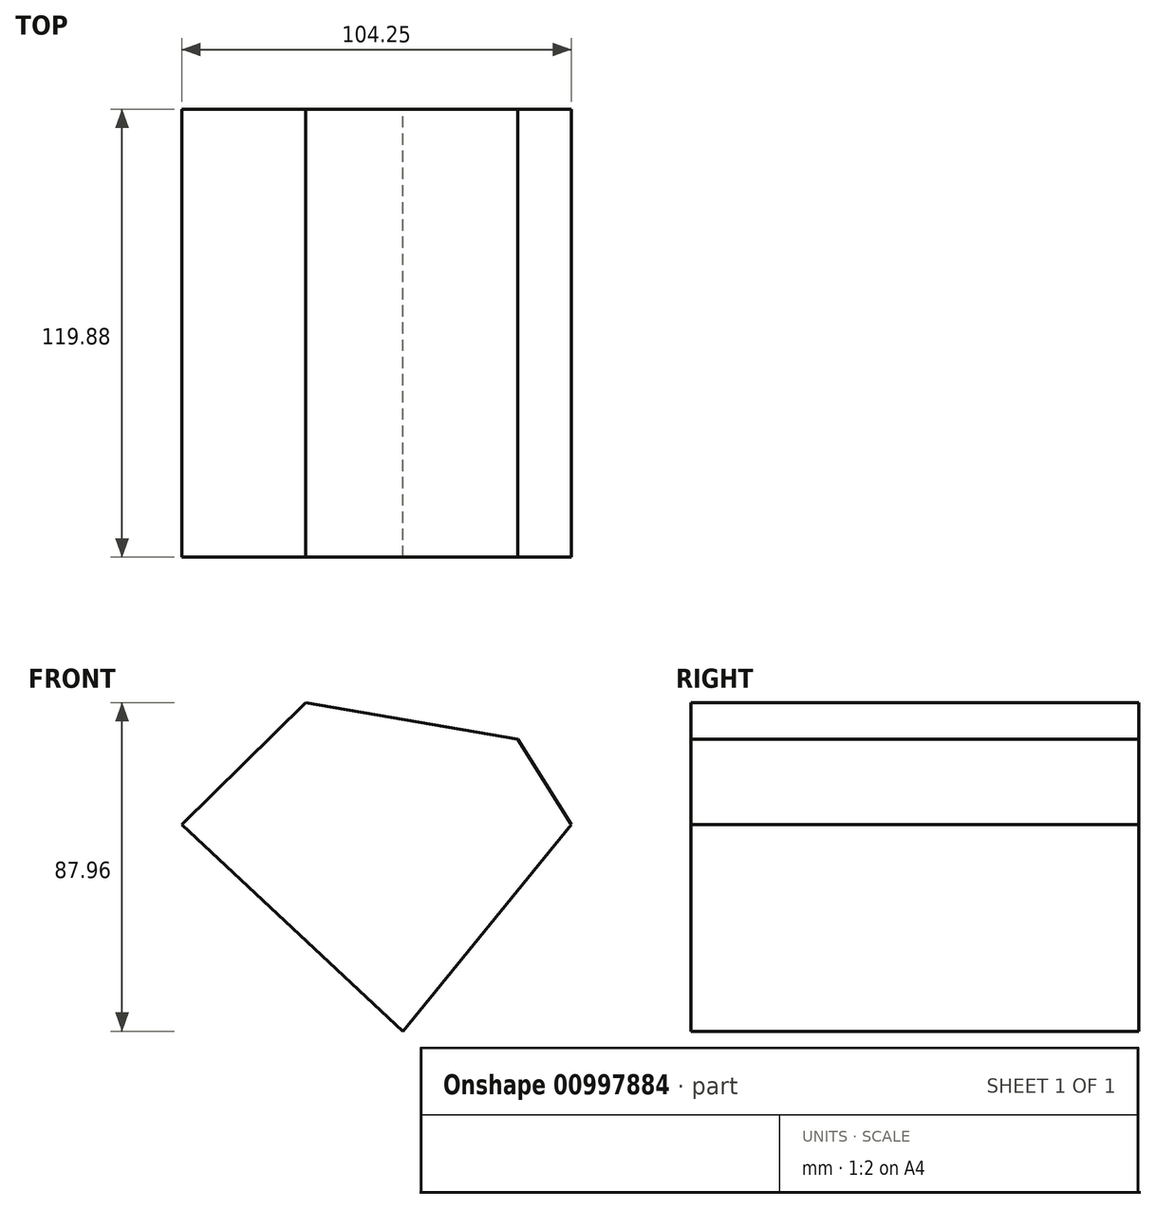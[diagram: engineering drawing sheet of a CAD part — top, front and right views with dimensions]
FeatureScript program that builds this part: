
annotation { "Feature Type Name" : "Feature", "Feature Type Description" : "" }
export const myFeature = defineFeature(function(context is Context, id is Id, definition is map)
    precondition{}
    {
        {
            var Q0;
            Q0=qCreatedBy(makeId("Front.planeOp"),FACE);
            var sketch = newSketch(context, id + "F0", { "sketchPlane" : qUnion([Q0])});
            skLineSegment(sketch, "E0", {"start": v(-59.12, 0) * mm, "end": v(-25.97, 32.58) * mm});
            skLineSegment(sketch, "E1", {"start": v(-25.97, 32.58) * mm, "end": v(30.76, 22.8) * mm});
            skLineSegment(sketch, "E2", {"start": v(30.76, 22.8) * mm, "end": v(45.13, 0) * mm});
            skLineSegment(sketch, "E3", {"start": v(45.13, 0) * mm, "end": v(0, -55.38) * mm});
            skLineSegment(sketch, "E4", {"start": v(0, -55.38) * mm, "end": v(-59.12, 0) * mm});
            skSolve(sketch);
        }
        {
            var Q0;
            Q0=makeQuery(id+"F0.imprint","IMPRINT",FACE,{"disambiguationData":[TD([[makeQuery(id+"F0.imprint","IMPRINT",EDGE,{"derivedFrom":sQuery(id+"F0.wireOp",EDGE,"E0")}),-1.0]])]});
            extrude(context, id + "F1", {"entities" : qUnion([Q0]), "endBound" : BoundingType.SYMMETRIC, "depth" : 119.89 * mm, "offsetDistance" : 25.4 * mm});
        }
    });
